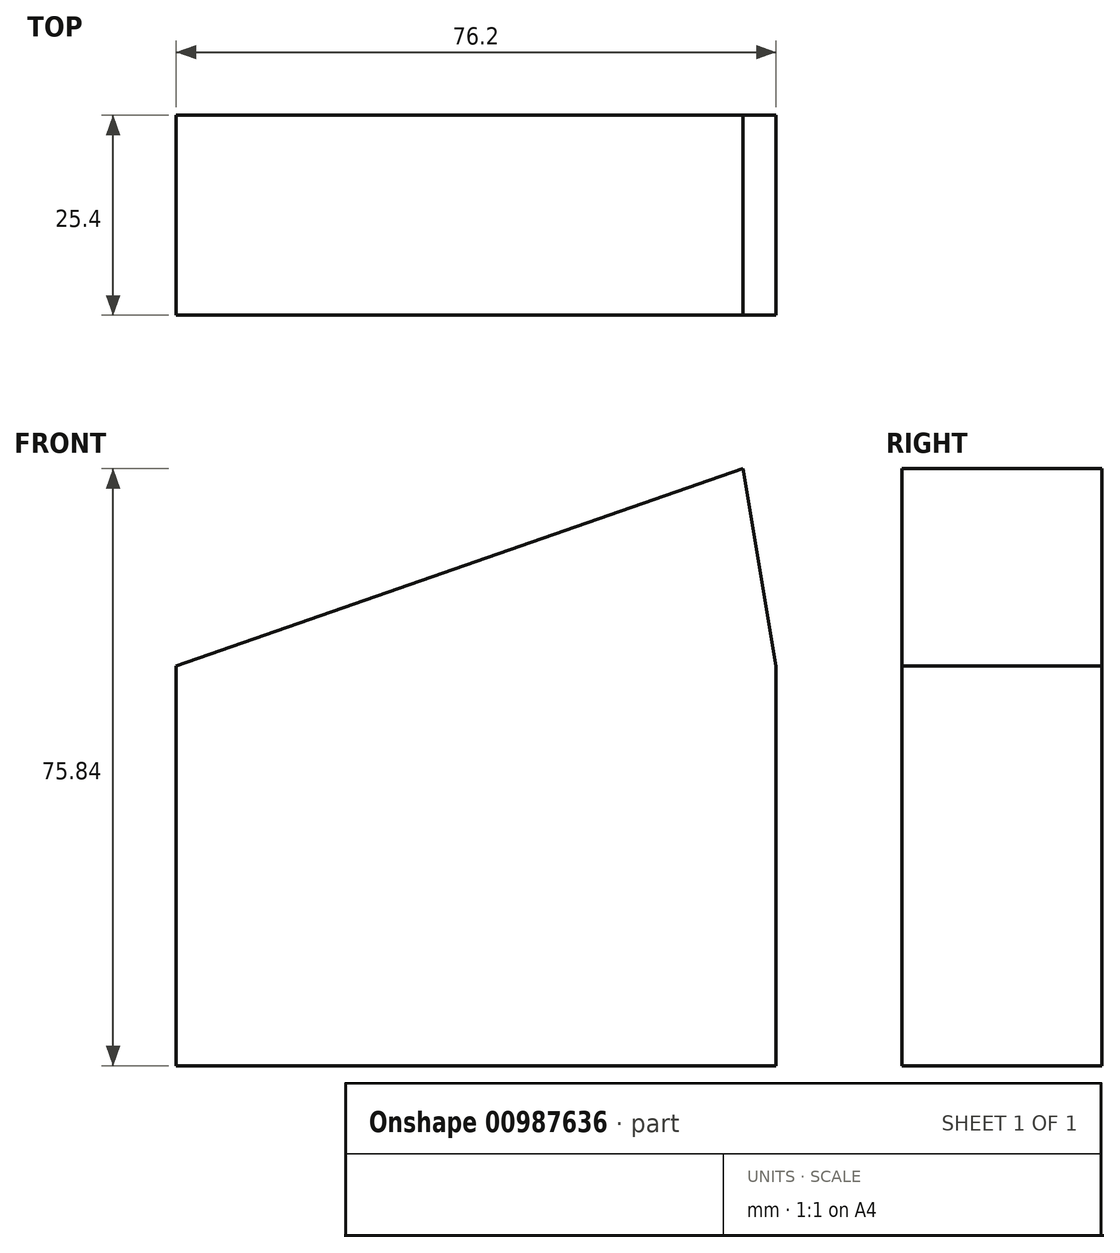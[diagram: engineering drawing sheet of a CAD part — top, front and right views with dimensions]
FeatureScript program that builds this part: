
annotation { "Feature Type Name" : "Feature", "Feature Type Description" : "" }
export const myFeature = defineFeature(function(context is Context, id is Id, definition is map)
    precondition{}
    {
        {
            var Q0;
            Q0=qCreatedBy(makeId("Front.planeOp"),FACE);
            var sketch = newSketch(context, id + "F0", { "sketchPlane" : qUnion([Q0])});
            skLineSegment(sketch, "E0.bottom", {"start": v(0, 0) * mm, "end": v(76.2, 0) * mm});
            skLineSegment(sketch, "E0.top", {"start": v(0, 50.8) * mm, "end": v(76.2, 50.8) * mm});
            skLineSegment(sketch, "E0.left", {"start": v(0, 0) * mm, "end": v(0, 50.8) * mm});
            skLineSegment(sketch, "E0.right", {"start": v(76.2, 0) * mm, "end": v(76.2, 50.8) * mm});
            skLineSegment(sketch, "E1", {"start": v(0, 50.8) * mm, "end": v(71.97, 75.84) * mm});
            skLineSegment(sketch, "E2", {"start": v(71.97, 75.84) * mm, "end": v(76.2, 50.8) * mm});
            skSolve(sketch);
        }
        {
            var Q0;
            Q0=makeQuery(id+"F0.imprint","IMPRINT",FACE,{"disambiguationData":[TD([[makeQuery(id+"F0.imprint","IMPRINT",EDGE,{"derivedFrom":sQuery(id+"F0.wireOp",EDGE,"E0.bottom")}),1.0]])]});
            var Q1;
            Q1=makeQuery(id+"F0.imprint","IMPRINT",FACE,{"disambiguationData":[TD([[makeQuery(id+"F0.imprint","IMPRINT",EDGE,{"derivedFrom":sQuery(id+"F0.wireOp",EDGE,"E0.top")}),1.0]])]});
            extrude(context, id + "F1", {"entities" : qUnion([Q0, Q1]), "depth" : 25.4 * mm, "offsetDistance" : 25.4 * mm});
        }
    });
